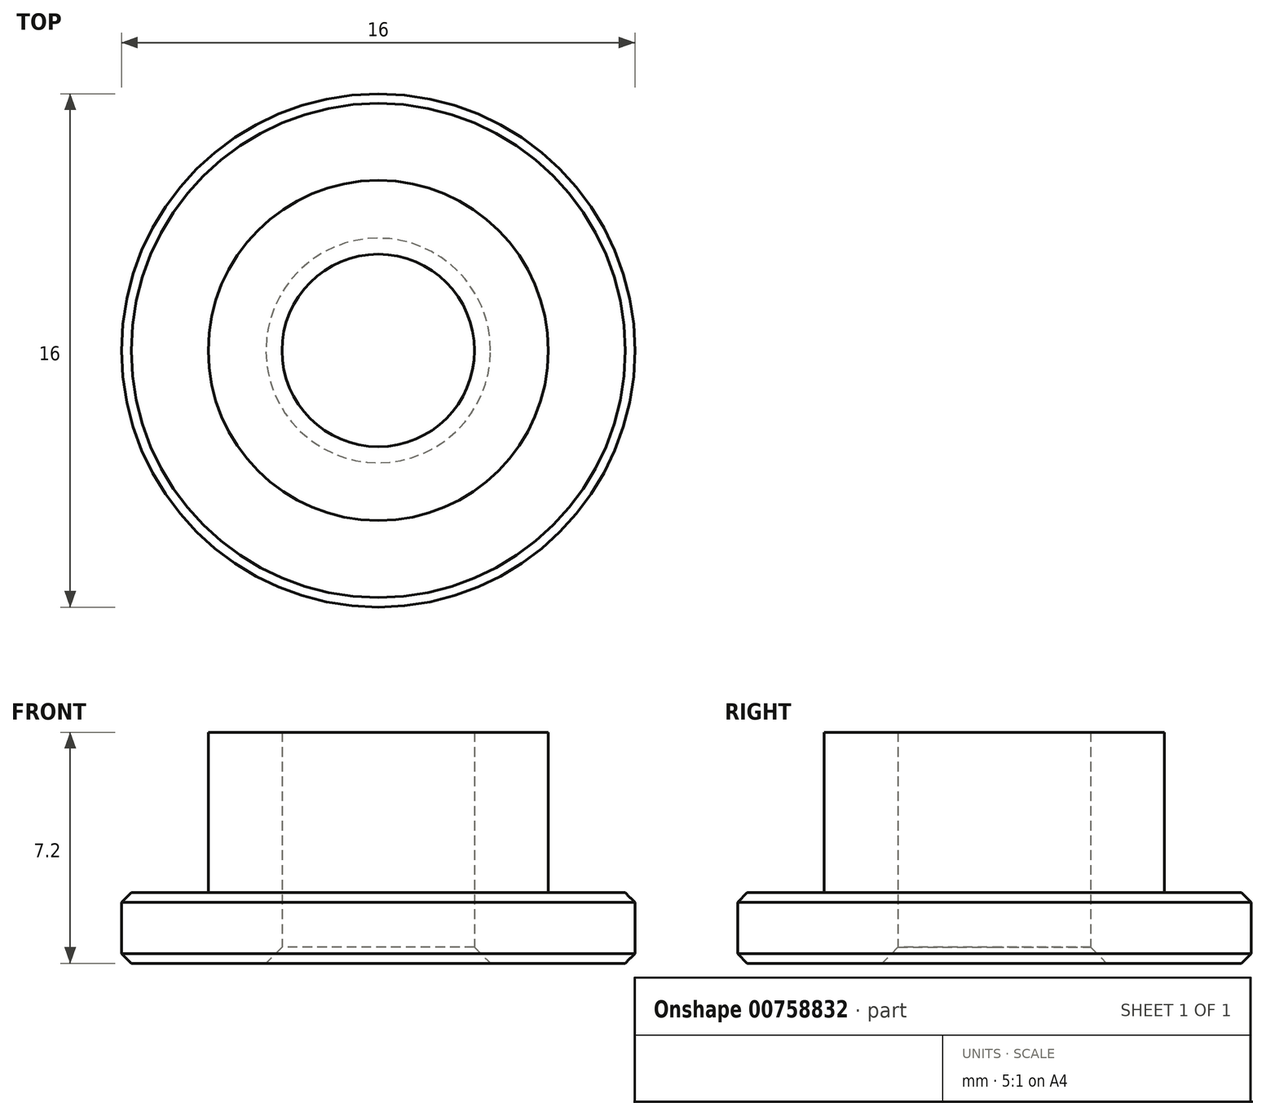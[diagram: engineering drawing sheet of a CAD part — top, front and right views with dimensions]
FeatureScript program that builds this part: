
annotation { "Feature Type Name" : "Feature", "Feature Type Description" : "" }
export const myFeature = defineFeature(function(context is Context, id is Id, definition is map)
    precondition{}
    {
        {
            var Q0;
            Q0=qCreatedBy(makeId("Top.planeOp"),FACE);
            var sketch = newSketch(context, id + "F0", { "sketchPlane" : qUnion([Q0])});
            skCircle(sketch, "E0", {"center": v(0, 0) * mm, "radius": 8 * mm});
            skCircle(sketch, "E1", {"center": v(0, 0) * mm, "radius": 5.3 * mm});
            skCircle(sketch, "E2", {"center": v(0, 0) * mm, "radius": 3 * mm});
            skSolve(sketch);
        }
        {
            var Q0;
            Q0=makeQuery(id+"F0.imprint","IMPRINT",FACE,{"disambiguationData":[TD([[makeQuery(id+"F0.imprint","IMPRINT",EDGE,{"derivedFrom":sQuery(id+"F0.wireOp",EDGE,"E1")}),1.0]])]});
            extrude(context, id + "F1", {"entities" : qUnion([Q0]), "depth" : 7.2 * mm, "offsetDistance" : 25 * mm});
        }
        {
            var Q0;
            Q0 = qSketchRegion(id + "F0", true);
            extrude(context, id + "F2", {"entities" : qUnion([Q0]), "operationType" : NewBodyOperationType.ADD, "depth" : 2.2 * mm, "offsetDistance" : 25 * mm});
        }
        {
            var Q0;
            Q0=makeQuery(id+"F1.opExtrude","CAP_EDGE",EDGE,{"disambiguationData":[OSD([sQuery(id+"F0.wireOp",EDGE,"E2")])],"isStart":true});
            chamfer(context, id + "F3", {"entities" : qUnion([Q0]), "width" : 0.5 * mm, "tangentPropagation" : true});
        }
        {
            var Q0;
            Q0=makeQuery(id+"F2.opExtrude","CAP_EDGE",EDGE,{"disambiguationData":[OSD([sQuery(id+"F0.wireOp",EDGE,"E0")])],"isStart":false});
            chamfer(context, id + "F4", {"entities" : qUnion([Q0]), "width" : 0.3 * mm, "tangentPropagation" : true});
        }
        {
            var Q0;
            Q0=makeQuery(id+"F2.opExtrude","CAP_EDGE",EDGE,{"disambiguationData":[OSD([sQuery(id+"F0.wireOp",EDGE,"E0")])],"isStart":true});
            chamfer(context, id + "F5", {"entities" : qUnion([Q0]), "width" : 0.3 * mm, "tangentPropagation" : true});
        }
    });
